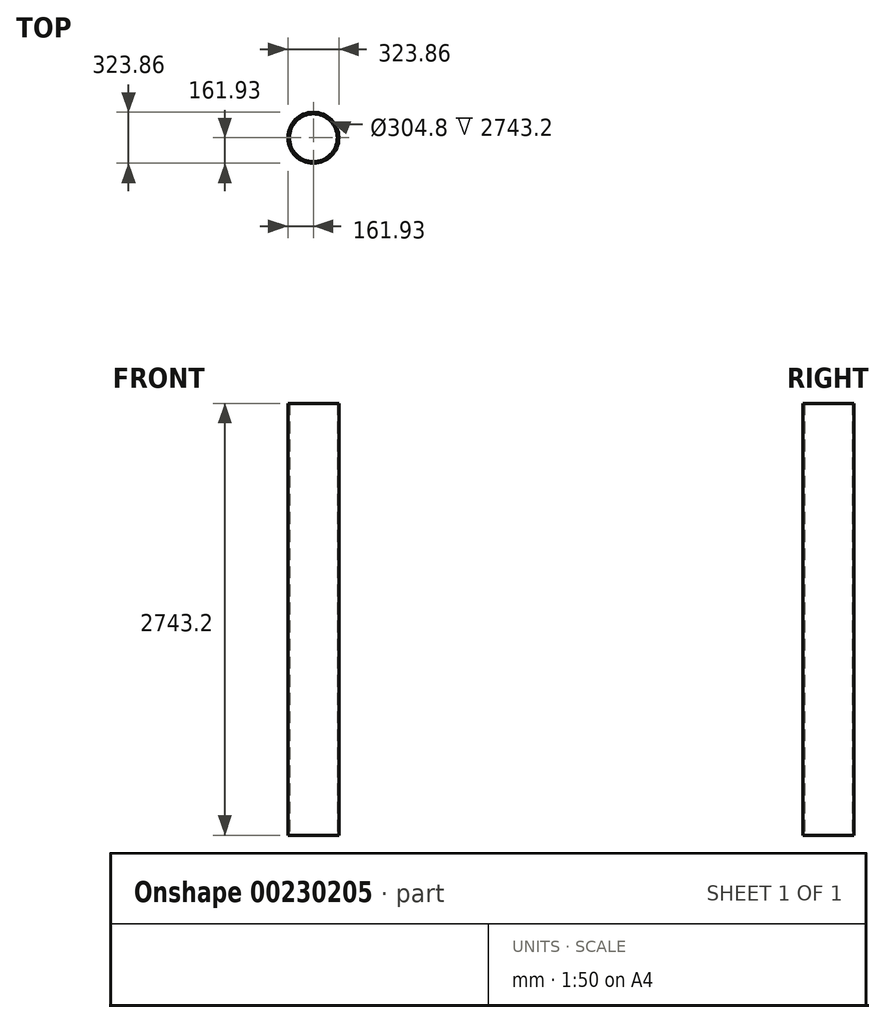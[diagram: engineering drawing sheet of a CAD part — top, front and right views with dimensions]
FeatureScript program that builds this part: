
annotation { "Feature Type Name" : "Feature", "Feature Type Description" : "" }
export const myFeature = defineFeature(function(context is Context, id is Id, definition is map)
    precondition{}
    {
        {
            var Q0;
            Q0=qCreatedBy(makeId("Top.planeOp"),FACE);
            var sketch = newSketch(context, id + "F0", { "sketchPlane" : qUnion([Q0])});
            skCircle(sketch, "E0", {"center": v(0, 0) * mm, "radius": 161.93 * mm});
            skCircle(sketch, "E1", {"center": v(0, 0) * mm, "radius": 152.4 * mm});
            skSolve(sketch);
        }
        {
            var Q0;
            Q0=qSketchRegion(id+"F0",true);
            extrude(context, id + "F1", {"entities" : qUnion([Q0]), "depth" : 2743.2 * mm});
        }
    });
